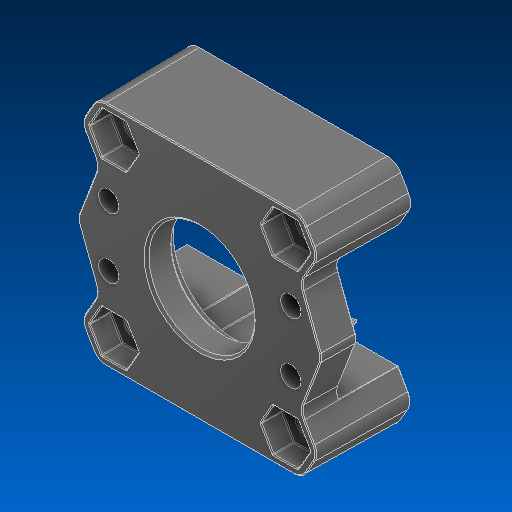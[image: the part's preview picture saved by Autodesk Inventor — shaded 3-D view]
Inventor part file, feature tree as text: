
AUTODESK INVENTOR PART (.ipt)
format: ipt  version: 2022.2 (Build 262287000, 287)  size: 2,112,000 bytes
history: native  units: in
note: dims shown in document units (in); Inventor stores cm internally (conversion verified against a paired STEP export)
features: chamfer x1
ambient origin geometry x8: Origin, YZ Plane, XZ Plane, XY Plane, X Axis, Y Axis, Z Axis, Center Point
bodies: Solid1 (feature_tree)
feature tree (1):
  chamfer  "Chamfer1"  [1 undecoded]
note: 1 required parameter value undecoded (feature->parameter linkage not recoverable at this tier; creation-order binding heuristic only, values carry confidence <= 0.55)
